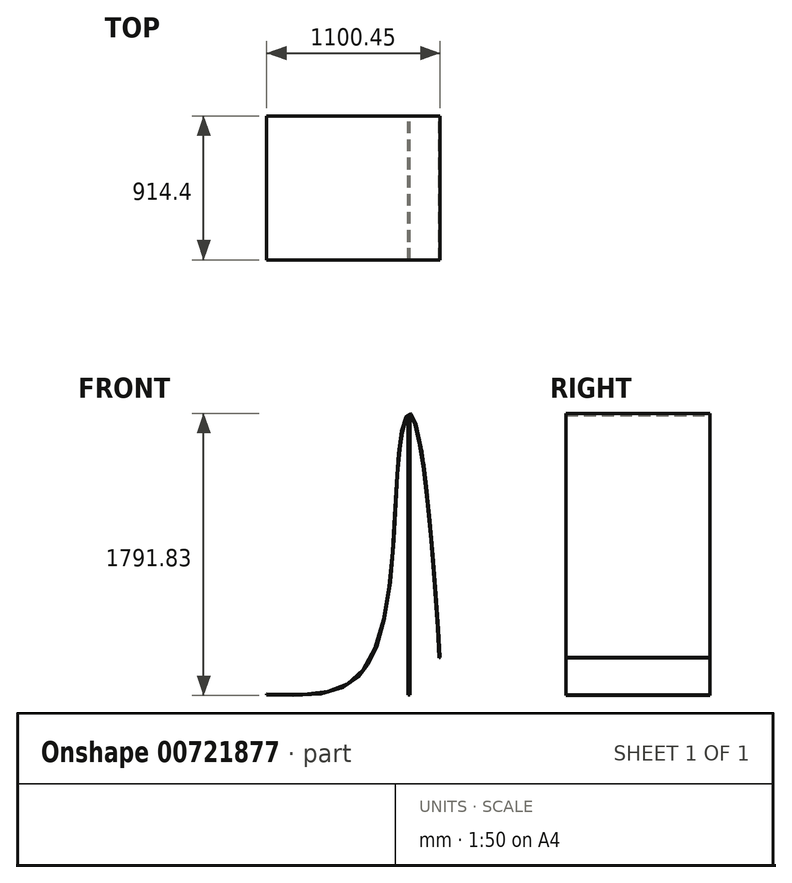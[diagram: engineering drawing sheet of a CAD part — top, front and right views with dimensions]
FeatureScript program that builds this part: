
annotation { "Feature Type Name" : "Feature", "Feature Type Description" : "" }
export const myFeature = defineFeature(function(context is Context, id is Id, definition is map)
    precondition{}
    {
        {
            var Q0;
            Q0=qCreatedBy(makeId("Front.planeOp"),FACE);
            var sketch = newSketch(context, id + "F0", { "sketchPlane" : qUnion([Q0])});
            skFitSpline(sketch, "E0", {"points": [v(-910.44, 0) * mm, v(-300.84, 147.98) * mm, v(-63.5, 1619.25) * mm, v(12.7, 1771.65) * mm, v(190, 229.92) * mm], "startDerivative": vector(2742.68, 0) * mm, "endDerivative": vector(158.87, -3425.9) * mm});
            skFitSpline(sketch, "E1.0", {"points": [v(-910.44, -6.35) * mm, v(-882, -6.35) * mm, v(-822.16, -7.99) * mm, v(-727.01, -10.54) * mm, v(-646.01, -8.7) * mm, v(-581.83, -2.38) * mm, v(-534.4, 5.4) * mm, v(-488.12, 16.84) * mm, v(-443.38, 32.58) * mm, v(-400.64, 53.25) * mm, v(-367.05, 75.1) * mm, v(-341.65, 95.65) * mm, v(-323.38, 112.68) * mm, v(-308.86, 128.27) * mm, v(-297.7, 141.62) * mm, v(-286.85, 155.56) * mm, v(-273.88, 174.07) * mm, v(-259.23, 197.93) * mm, v(-245.45, 223.36) * mm, v(-228.2, 259.25) * mm, v(-208.64, 307.65) * mm, v(-188.12, 370.77) * mm, v(-170.3, 438.31) * mm, v(-149.82, 533.46) * mm, v(-129.73, 660.38) * mm, v(-112.58, 820.52) * mm, v(-100.48, 983.51) * mm, v(-93.07, 1117.56) * mm, v(-87.8, 1221.22) * mm, v(-83.95, 1296.56) * mm, v(-79.97, 1368.85) * mm, v(-75.62, 1437.46) * mm, v(-70.68, 1501.77) * mm, v(-65.87, 1551.24) * mm, v(-61.5, 1588.03) * mm, v(-57.93, 1614.13) * mm, v(-54.05, 1638.68) * mm, v(-49.85, 1661.59) * mm, v(-45.39, 1682.74) * mm, v(-40.68, 1702.02) * mm, v(-35.75, 1719.34) * mm, v(-30.65, 1734.56) * mm, v(-25.43, 1747.57) * mm, v(-20.14, 1758.23) * mm, v(-15.77, 1765.01) * mm, v(-12.42, 1769.1) * mm, v(-10.02, 1771.48) * mm, v(-7.8, 1773.19) * mm, v(-5.83, 1774.26) * mm, v(-4.13, 1774.8) * mm, v(-2.64, 1774.93) * mm, v(-1.14, 1774.73) * mm, v(0.58, 1774.12) * mm, v(2.6, 1772.9) * mm, v(4.88, 1770.98) * mm, v(7.36, 1768.27) * mm, v(9.97, 1764.73) * mm, v(12.68, 1760.38) * mm, v(16.37, 1753.52) * mm, v(21.06, 1743.07) * mm, v(26.72, 1727.68) * mm, v(32.38, 1709.63) * mm, v(38.01, 1689.06) * mm, v(43.6, 1666.1) * mm, v(51, 1632.47) * mm, v(60.1, 1585.09) * mm, v(70.77, 1520.65) * mm, v(81.14, 1449.6) * mm, v(91.2, 1372.86) * mm, v(100.92, 1291.39) * mm, v(113.37, 1177.7) * mm, v(127.94, 1028.46) * mm, v(143.62, 845.44) * mm, v(157.3, 666) * mm, v(168.74, 497.62) * mm, v(177.76, 347.8) * mm, v(182.01, 265.29) * mm, v(183.66, 229.62) * mm]});
            skLineSegment(sketch, "E2", {"start": v(-910.44, -6.35) * mm, "end": v(-910.44, 0) * mm});
            skLineSegment(sketch, "E3", {"start": v(183.66, 229.62) * mm, "end": v(190, 229.92) * mm});
            skLineSegment(sketch, "E4", {"start": v(12.7, 1771.65) * mm, "end": v(12.7, -6.35) * mm, "construction": true});
            skLineSegment(sketch, "E5.bottom", {"start": v(-12.7, -6.35) * mm, "end": v(0, -6.35) * mm});
            skLineSegment(sketch, "E5.top", {"start": v(-12.7, 1768.47) * mm, "end": v(0, 1768.47) * mm});
            skLineSegment(sketch, "E5.left", {"start": v(-12.7, -6.35) * mm, "end": v(-12.7, 1768.47) * mm});
            skLineSegment(sketch, "E5.right", {"start": v(0, -6.35) * mm, "end": v(0, 1768.47) * mm});
            skLineSegment(sketch, "E6", {"start": v(-456.11, -6.35) * mm, "end": v(12.7, -6.35) * mm, "construction": true});
            skSolve(sketch);
        }
        {
            var Q0;
            Q0 = qSketchRegion(id + "F0", true);
            extrude(context, id + "F1", {"entities" : qUnion([Q0]), "depth" : 914.4 * mm, "offsetDistance" : 25.4 * mm});
        }
    });
